# Revit family: Duct_Outlet-Unico-Round
name_source: partatom
category: Duct Accessories
units: mm (PartAtom-declared; Revit-internal decimal feet)

## family parameters
Always vertical = No
Cut with Voids When Loaded = No
OmniClass Number = 23.75.70.00
OmniClass Title = HVAC Distribution Devices
Part Type = Attaches To
Round Connector Dimension = Use Diameter
Shared = No
Work Plane-Based = Yes

## types (40) — shared parameters
Assembly Code = D3040100
Default Elevation = 48"
Description = Round Outlet
Keynote = 23 30 00
Manufacturer = Unico, Inc.
Manufacturer Fax Number = 314-457-9000
Performance URL = https://www.unicosystem.com
Product Page URL = https://www.unicosystem.com
URL = https://www.unicosystem.com
Version = 2020 - v1.0a
Video Link = https://www.youtube.com
Warranty URL = https://www.unicosystem.com

## per-type parameters (varying)
| type | C Connector Offset | Constraints | Duct Connection Diameter | Finish | Height | Width |
| UPC-256 | 1" | 1 | 3" | Paint - Unico - White | 0" | 5 1/2" |
| UPC-256-BLK | 1" | 1 | 3" | Paint - Unico - Black | 0" | 5 1/2" |
| UPC-256-CHR | 1" | 1 | 3" | Metal - Unico - Chrome | 0" | 5 1/2" |
| UPC-256-BRS | 1" | 1 | 3" | Metal - Unico - Brass | 0" | 5 1/2" |
| UPC-56TB | 0" | 5 | 3" | Paint - Unico - White | 0" | 5 1/16" |
| UPC-56TB-BLK | 0" | 5 | 3" | Paint - Unico - Black | 0" | 5 1/16" |
| UPC-56TB-CHR | 0" | 5 | 3" | Metal - Unico - Chrome | 0" | 5 1/16" |
| UPC-56TB-BRS | 0" | 5 | 3" | Metal - Unico - Brass | 0" | 5 1/16" |
| UPC-57T-WO | 0" | 6 | 3" | Wood - Unico - White Oak | 1/16" | 5" |
| UPC-57T-WL | 0" | 6 | 3" | Wood - Unico - Walnut | 1/16" | 5" |
| UPC-57T-RO | 0" | 6 | 3" | Wood - Unico - Red Oak | 1/16" | 5" |
| UPC-57T-PO | 0" | 6 | 3" | Wood - Unico - Poplar | 1/16" | 5" |
| UPC-57T-PI | 0" | 6 | 3" | Wood - Unico - Pine | 1/16" | 5" |
| UPC-57T-MA | 0" | 6 | 3" | Wood - Unico - Maple | 1/16" | 5" |
| UPC-57T-MH | 0" | 6 | 3" | Wood - Unico - Mahogany | 1/16" | 5" |
| UPC-57T-K | 0" | 6 | 3" | Wood - Unico - Knotted Pine | 1/16" | 5" |
| UPC-57T-C | 0" | 6 | 3" | Wood - Unico - Cherry | 1/16" | 5" |
| UPC-57T-B | 0" | 6 | 3" | Wood - Unico - Birch | 1/16" | 5" |
| UPC-57T-WO-F | 0" | 7 | 3" | Wood - Unico - White Oak | 1/16" | 5" |
| UPC-57T-WL-F | 0" | 7 | 3" | Wood - Unico - Walnut | 1/16" | 5" |
| UPC-57T-RO-F | 0" | 7 | 3" | Wood - Unico - Red Oak | 1/16" | 5" |
| UPC-57T-PO-F | 0" | 7 | 3" | Wood - Unico - Poplar | 1/16" | 5" |
| UPC-57T-PI-F | 0" | 7 | 3" | Wood - Unico - Pine | 1/16" | 5" |
| UPC-57T-MA-F | 0" | 7 | 3" | Wood - Unico - Maple | 1/16" | 5" |
| UPC-57T-MH-F | 0" | 7 | 3" | Wood - Unico - Mahogany | 1/16" | 5" |
| UPC-57T-K-F | 0" | 7 | 3" | Wood - Unico - Knotted Pine | 1/16" | 5" |
| UPC-57T-C-F | 0" | 7 | 3" | Wood - Unico - Cherry | 1/16" | 5" |
| UPC-57T-B-F | 0" | 7 | 3" | Wood - Unico - Birch | 1/16" | 5" |
| UPC-257-WO | 1 1/4" | 4 | 3" | Wood - Unico - White Oak | 0" | 5 1/2" |
| UPC-257-WL | 1 1/4" | 4 | 3" | Wood - Unico - Walnut | 0" | 5 1/2" |
| UPC-257-RO | 1 1/4" | 4 | 3" | Wood - Unico - Red Oak | 0" | 5 1/2" |
| UPC-257-PO | 1 1/4" | 4 | 3" | Wood - Unico - Poplar | 0" | 5 1/2" |
| UPC-257-PI | 1 1/4" | 4 | 3" | Wood - Unico - Pine | 0" | 5 1/2" |
| UPC-257-MA | 1 1/4" | 4 | 3" | Wood - Unico - Maple | 0" | 5 1/2" |
| UPC-257-MH | 1 1/4" | 4 | 3" | Wood - Unico - Mahogany | 0" | 5 1/2" |
| UPC-257-K | 1 1/4" | 4 | 3" | Wood - Unico - Knotted Pine | 0" | 5 1/2" |
| UPC-257-C | 1 1/4" | 4 | 3" | Wood - Unico - Cherry | 0" | 5 1/2" |
| UPC-257-B | 1 1/4" | 4 | 3" | Wood - Unico - Birch | 0" | 5 1/2" |
| UPC-58-15 | 0" | 2 | 2" | Paint - Unico - White | 0" | 5" |
| UPC-58-25 | 0" | 3 | 2" | Paint - Unico - White | 0" | 5 1/2" |

note: column(s) folded — value = type name in every type: Model

## geometry (parser evidence)
native form markers: Sweep x5
no freeform markers — native parametric forms only
